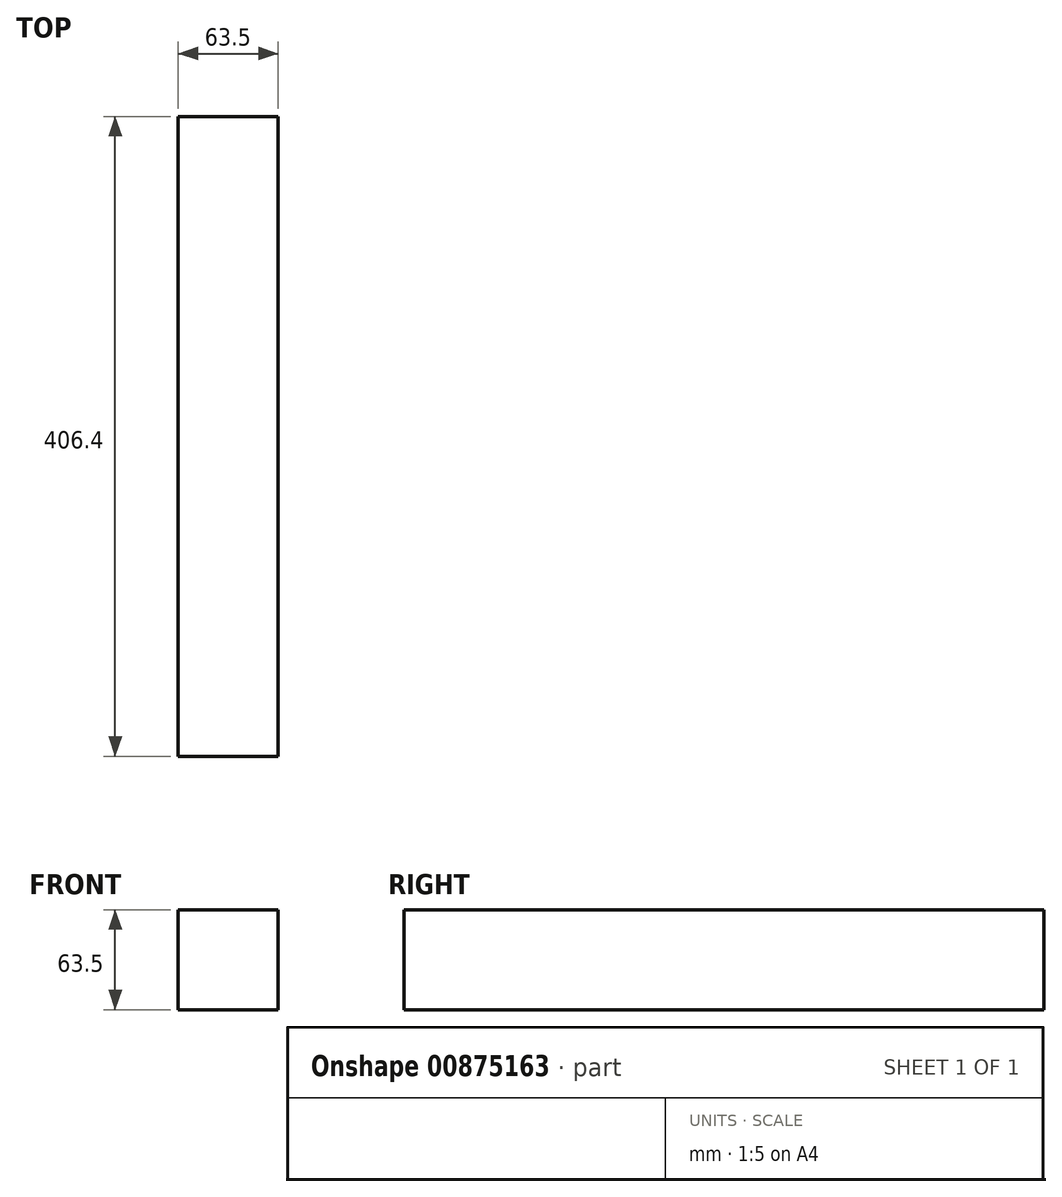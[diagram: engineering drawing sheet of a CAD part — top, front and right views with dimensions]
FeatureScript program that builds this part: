
annotation { "Feature Type Name" : "Feature", "Feature Type Description" : "" }
export const myFeature = defineFeature(function(context is Context, id is Id, definition is map)
    precondition{}
    {
        {
            var Q0;
            Q0=qCreatedBy(makeId("Front.planeOp"),FACE);
            var sketch = newSketch(context, id + "F0", { "sketchPlane" : qUnion([Q0])});
            skLineSegment(sketch, "E0.bottom", {"start": v(-164.57, 68.12) * mm, "end": v(-101.07, 68.12) * mm});
            skLineSegment(sketch, "E0.top", {"start": v(-164.57, 4.62) * mm, "end": v(-101.07, 4.62) * mm});
            skLineSegment(sketch, "E0.left", {"start": v(-164.57, 68.12) * mm, "end": v(-164.57, 4.62) * mm});
            skLineSegment(sketch, "E0.right", {"start": v(-101.07, 68.12) * mm, "end": v(-101.07, 4.62) * mm});
            skSolve(sketch);
        }
        {
            var Q0;
            Q0=makeQuery(id+"F0.imprint","IMPRINT",FACE,{"disambiguationData":[TD([[makeQuery(id+"F0.imprint","IMPRINT",EDGE,{"derivedFrom":sQuery(id+"F0.wireOp",EDGE,"E0.bottom")}),-1.0]])]});
            extrude(context, id + "F1", {"entities" : qUnion([Q0]), "depth" : 1498.6 * mm, "offsetDistance" : 25.4 * mm});
        }
        {
            var Q0;
            Q0=makeQuery(id+"F1.opExtrude","CAP_FACE",FACE,{"disambiguationData":[OSD([sQuery(id+"F0.wireOp",EDGE,"E0.bottom"),sQuery(id+"F0.wireOp",EDGE,"E0.top"),sQuery(id+"F0.wireOp",EDGE,"E0.left"),sQuery(id+"F0.wireOp",EDGE,"E0.right")])],"isStart":true});
            extrude(context, id + "F2", {"entities" : qUnion([Q0]), "operationType" : NewBodyOperationType.REMOVE, "oppositeDirection" : true, "depth" : 1092.2 * mm, "offsetDistance" : 25.4 * mm});
        }
    });
